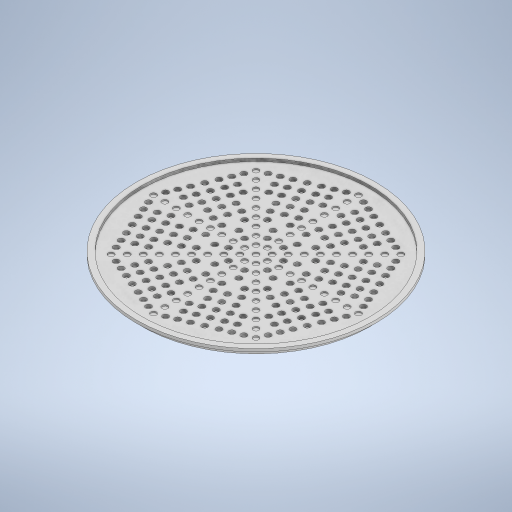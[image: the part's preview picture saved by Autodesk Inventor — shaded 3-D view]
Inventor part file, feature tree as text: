
AUTODESK INVENTOR PART (.ipt)
format: ipt  version: 2023 (Build 270158030, 158C)  size: 869,888 bytes
history: native  units: in
note: dims shown in document units (in); Inventor stores cm internally (conversion verified against a paired STEP export)
features: extrude x5, sketch x5, projected_geometry x5, pattern_circular x2, pattern_linear x1
ambient origin geometry x8: Origin, YZ Plane, XZ Plane, XY Plane, X Axis, Y Axis, Z Axis, Center Point
bodies: Solid1 (feature_tree)
feature tree (18):
  extrude  "Extrusion1"  Depth=0.05in TaperAngle=0.0deg
  extrude  "Extrusion2"  Depth=2.1in
  extrude  "Extrusion3"  Depth=0.25in
  extrude  "Extrusion4"  Depth=0.125in
  pattern_linear  "Rectangular Pattern1"  Spacing1=0.01in  [1 undecoded]
  pattern_circular  "Circular Pattern1"  [2 undecoded]
  extrude  "Extrusion5"  Depth=0.01in TaperAngle=0.0deg
  pattern_circular  "Circular Pattern2"  Count=10  [1 undecoded]
  sketch  "Sketch1"  dims[d0=2.0in d1=0.05in d2=0.0in]
  sketch  "Sketch2"  dims[d3=2.0in d4=2.1in]
  sketch  "Sketch3"  dims[d5=0.025in d6=0.0in d7=0.25in]
  sketch  "Sketch4"  dims[d8=0.25in d9=0.125in]
  sketch  "Sketch5"  dims[d10=0.1875in d11=0.01in d12=0.0in d13=0.05in d14=0.01in d15=0.0in d16=3.937in d18=0.1in d19=3.1496in d20=360.0deg d22=0.05in d23=0.05in d24=0.05in d25=0.05in d26=0.05in d27=0.05in d28=0.05in d29=67.5deg d30=67.5deg d31=0.05in d32=0.05in d33=0.05in d34=0.05in d35=0.05in d36=0.05in d37=0.05in d38=0.05in d39=0.05in d40=0.05in d41=0.05in d42=67.5deg d43=67.5deg d44=0.05in d45=0.05in d46=0.05in d47=0.05in d48=0.05in d49=0.05in d50=0.05in d51=0.05in d52=0.05in d53=0.025in d54=0.0in d55=3.1496in d56=360.0deg]
  projected_geometry  "Projected Loop1"
  projected_geometry  "Projected Loop2"
  projected_geometry  "Projected Loop3"
  projected_geometry  "Projected Loop4"
  projected_geometry  "Projected Loop5"
note: 4 required parameter values undecoded (feature->parameter linkage not recoverable at this tier; creation-order binding heuristic only, values carry confidence <= 0.55)
